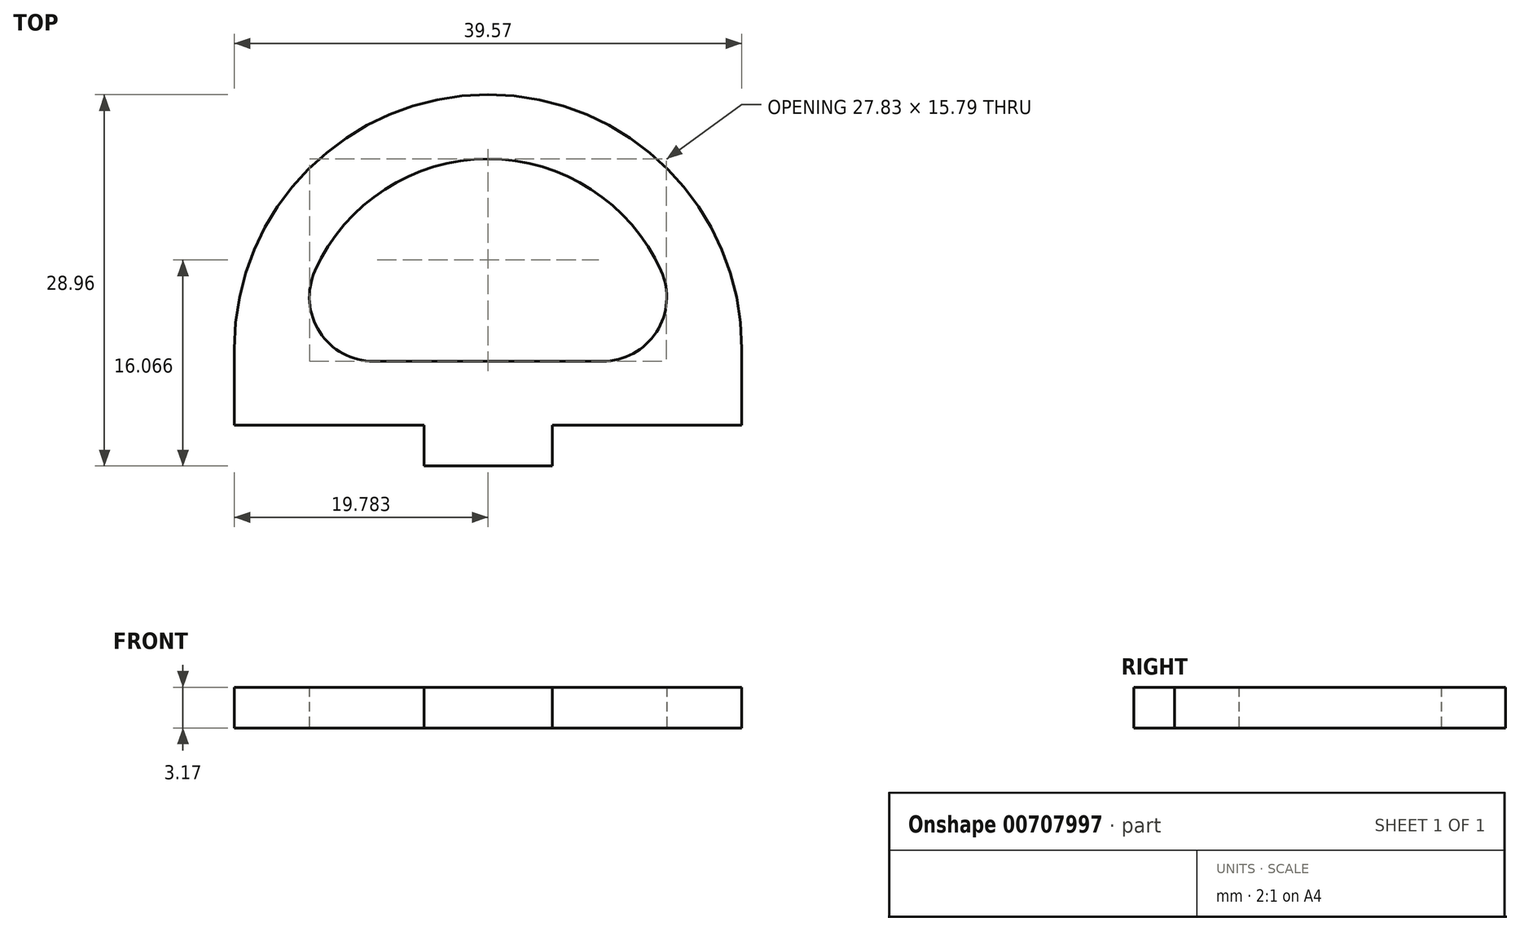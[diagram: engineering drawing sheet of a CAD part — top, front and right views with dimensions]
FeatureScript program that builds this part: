
annotation { "Feature Type Name" : "Feature", "Feature Type Description" : "" }
export const myFeature = defineFeature(function(context is Context, id is Id, definition is map)
    precondition{}
    {
        {
            var Q0;
            Q0=qCreatedBy(makeId("Top.planeOp"), FACE);
            var sketch = newSketch(context, id + "F0", { "sketchPlane" : qUnion([Q0])});
            skPoint(sketch, "E0.0", {"position": v(-19.06, -4.57) * mm});
            skPoint(sketch, "E1.0", {"position": v(-4.28, -4.57) * mm});
            skPoint(sketch, "E2.0", {"position": v(5.72, -4.57) * mm});
            skPoint(sketch, "E3.0", {"position": v(20.51, -4.57) * mm});
            skLineSegment(sketch, "E4", {"start": v(-19.06, -4.57) * mm, "end": v(-4.28, -4.57) * mm});
            skLineSegment(sketch, "E5", {"start": v(-4.28, -4.57) * mm, "end": v(-4.28, -7.74) * mm});
            skLineSegment(sketch, "E6", {"start": v(-4.28, -7.74) * mm, "end": v(5.72, -7.74) * mm});
            skLineSegment(sketch, "E7", {"start": v(5.72, -7.74) * mm, "end": v(5.72, -4.57) * mm});
            skLineSegment(sketch, "E8", {"start": v(5.72, -4.57) * mm, "end": v(20.51, -4.57) * mm});
            skLineSegment(sketch, "E9", {"start": v(-19.06, -4.57) * mm, "end": v(-19.06, 1.43) * mm});
            skLineSegment(sketch, "E10", {"start": v(20.51, 1.43) * mm, "end": v(20.51, -4.57) * mm});
            skArc(sketch, "E11", {"start": v(20.51, 1.43) * mm, "mid": v(0.72, 21.22) * mm, "end": v(-19.06, 1.43) * mm});
            skLineSegment(sketch, "E12.0", {"start": v(5.72, 0.43) * mm, "end": v(9.66, 0.43) * mm});
            skArc(sketch, "E12.2", {"start": v(14.22, 7.48) * mm, "mid": v(0.72, 16.22) * mm, "end": v(-12.77, 7.48) * mm});
            skLineSegment(sketch, "E12.4", {"start": v(-8.2, 0.43) * mm, "end": v(-4.28, 0.43) * mm});
            skLineSegment(sketch, "E13", {"start": v(-4.28, 0.43) * mm, "end": v(5.72, 0.43) * mm});
            skArc(sketch, "E14.filletArc", {"start": v(-12.77, 7.48) * mm, "mid": v(-12.4, 2.71) * mm, "end": v(-8.2, 0.43) * mm});
            skArc(sketch, "E15.filletArc", {"start": v(9.66, 0.43) * mm, "mid": v(13.85, 2.71) * mm, "end": v(14.22, 7.48) * mm});
            skSolve(sketch);
        }
        {
            var Q0;
            Q0 = qSketchRegion(id + "F0", true);
            extrude(context, id + "F1", {"entities" : qUnion([Q0]), "depth" : 3.17 * mm, "offsetDistance" : 25 * mm});
        }
    });
